# Revit family: Haworth_Compose_Panel_DoorSliding
name_source: partatom
category: Furniture Systems
revit_build: Autodesk Revit 2018 (Build: 20170223_1515(x64)
units: mm (PartAtom-declared; Revit-internal decimal feet)

## family parameters
Always vertical = Yes
Cut with Voids When Loaded = No
OmniClass Number = 23.40.70.14.64.21
OmniClass Title = Systems Furniture
Part Type = Normal
Room Calculation Point = No
Round Connector Dimension = Use Diameter
Shared = No
Work Plane-Based = No

## types (6) — shared parameters
Assembly Code = E2020500
Bottom Rail Width = 4 1/4"
Description = Haworth Compose Panel Door Sliding
Door Finish = Haworth _ Paint _ Putty
Door Offset = 1/2"
Glass Finish = Haworth _ Glass _ Clear
Glass Offset = 4 1/4"
Manufacturer = Haworth
Max. Height = 82"
Max. Width = 42"
Min. Height = 66"
Min. Width = 36"
Min/Max Height = 66, 74, 82 in.
Min/Max Width = 36, 42 in.
Model = VUZF
Panel Depth = 1/2"
Revision Number = 4
Size = Verify Final Dim. w/ Haworth
Style Width = 2 3/4"
Sustainability Info = http://media.haworth.com
Top Rail Width = 2 3/4"
Track Finish = Haworth _ Polymer _ Black
URL = http://www.haworth.com
URL - Product = http://www.haworth.com
Warranty = http://www.haworth.com

## per-type parameters (varying)
| type | Actual Height | Actual Width | Door Height | Height | Panel Height | Panel Width | Pull Height Centerline | Sliding Track Length | Width |
| 66h 36w | 66 1/2" | 36" | 66" | 66" | 59" | 30 1/2" | 33 1/4" | 75" | 36" |
| 74h 36w | 74 1/2" | 36" | 74" | 74" | 67" | 30 1/2" | 37 1/4" | 75" | 36" |
| 82h 36w | 82 1/2" | 36" | 82" | 82" | 75" | 30 1/2" | 41 1/4" | 75" | 36" |
| 82h 42w | 82 1/2" | 42" | 82" | 82" | 75" | 36 1/2" | 41 1/4" | 87" | 42" |
| 74h 42w | 74 1/2" | 42" | 74" | 74" | 67" | 36 1/2" | 37 1/4" | 87" | 42" |
| 66h 42w | 66 1/2" | 42" | 66" | 66" | 59" | 36 1/2" | 33 1/4" | 87" | 42" |

## geometry (parser evidence)
native form markers: Sweep x11
no freeform markers — native parametric forms only
